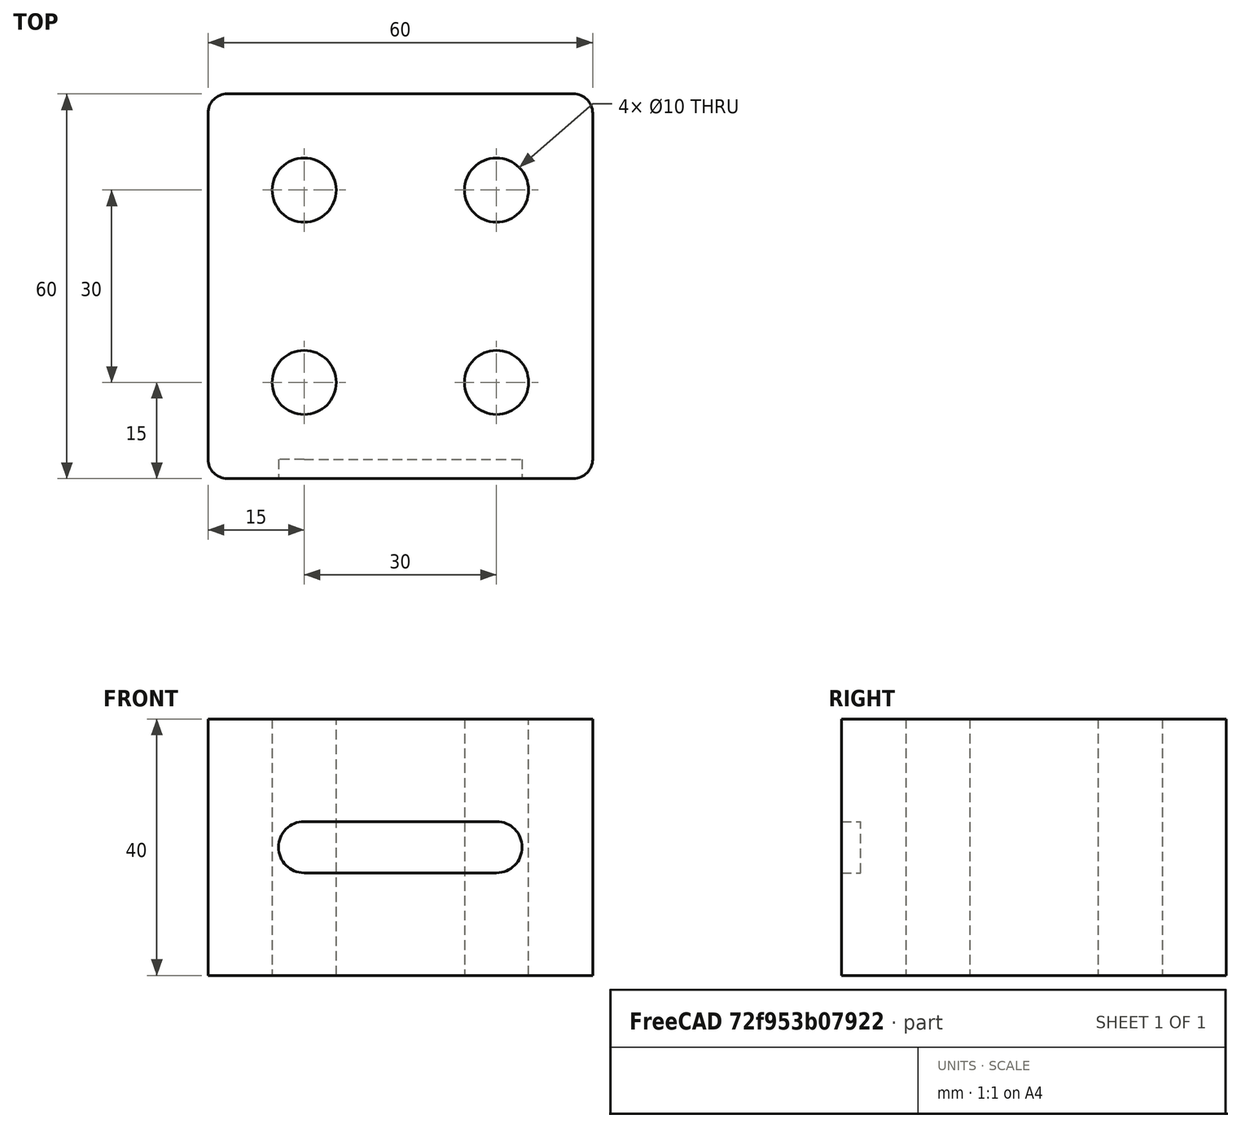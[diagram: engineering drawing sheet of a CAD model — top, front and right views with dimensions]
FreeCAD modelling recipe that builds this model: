
FCSTD DOCUMENT  (FreeCAD 1.0R39319 (Git))
Label: block(2D drawing)
License: All rights reserved
LicenseURL: https://en.wikipedia.org/wiki/All_rights_reserved
objects: TechDraw::DrawViewDimension×6, TechDraw::DrawProjGroupItem×4, TechDraw::DrawViewBalloon×3, Sketcher::SketchObject×2, TechDraw::DrawViewAnnotation×2, PartDesign::Pad×1, PartDesign::Pocket×1, PartDesign::Fillet×1, PartDesign::Body×1, TechDraw::DrawSVGTemplate×1, TechDraw::DrawProjGroup×1, TechDraw::DrawPage×1
note: 21 computed .brp shape members not serialized (recipe doc carries the construction recipe); baked Part::Feature solids carry a one-line shape summary decoded from their .brp

FEATURE [Sketcher::SketchObject] Sketch
  ArcFitTolerance = 1e-06
  AttachmentSupport = -> [XY_Plane]
  FullyConstrained = true
  MakeInternals = false
  MapMode = 5
  sketch-geometry (9):
    g0: LineSegment StartX=-30 StartY=30 StartZ=0 EndX=-30 EndY=-30 EndZ=0
    g1: LineSegment StartX=-30 StartY=-30 StartZ=0 EndX=30 EndY=-30 EndZ=0
    g2: LineSegment StartX=30 StartY=-30 StartZ=0 EndX=30 EndY=30 EndZ=0
    g3: LineSegment StartX=30 StartY=30 StartZ=0 EndX=-30 EndY=30 EndZ=0
    g4: GeomPoint [constr] X=0 Y=0 Z=0
    g5: Circle CenterX=-15 CenterY=15 CenterZ=0 NormalX=0 NormalY=0 NormalZ=1 AngleXU=0 Radius=5
    g6: Circle CenterX=15 CenterY=15 CenterZ=0 NormalX=0 NormalY=0 NormalZ=1 AngleXU=0 Radius=5
    g7: Circle CenterX=-15 CenterY=-15 CenterZ=0 NormalX=0 NormalY=0 NormalZ=1 AngleXU=0 Radius=5
    g8: Circle CenterX=15 CenterY=-15 CenterZ=0 NormalX=0 NormalY=0 NormalZ=1 AngleXU=0 Radius=5
  constraints (24):
    c: Coincident(g0,g1)
    c: Coincident(g1,g2)
    c: Coincident(g2,g3)
    c: Coincident(g3,g0)
    c: Vertical(g0)
    c: Vertical(g2)
    c: Horizontal(g1)
    c: Horizontal(g3)
    c: Symmetric(g2,g0,g4)
    c: Coincident(g4,g-1)
    c: DistanceX(g3,g3) = 60
    c: Equal(g3,g2)
    c: Distance(g5,g3) = 15
    c: Distance(g5,g0) = 15
    c: Diameter(g5) = 10
    c: Vertical(g5,g7)
    c: Horizontal(g7,g8)
    c: Vertical(g6,g8)
    c: Distance(g6,g3) = 15
    c: Distance(g8,g2) = 15
    c: Distance(g7,g1) = 15
    c: Equal(g5,g6)
    c: Equal(g6,g8)
    c: Equal(g8,g7)
FEATURE [PartDesign::Pad] Pad
  Direction = (0,0,1)
  Length = 40
  Length2 = 10
  Profile = -> Sketch
  ReferenceAxis = -> Sketch [N_Axis]
  Refine = true
  Suppressed = false
  Type = 0
FEATURE [Sketcher::SketchObject] Sketch001
  ArcFitTolerance = 1e-06
  AttachmentSupport = -> [Pad]
  FullyConstrained = true
  MakeInternals = false
  MapMode = 5
  Placement = pos=(0,-30,0) rot=(1,0,0;1.5708rad)
  sketch-geometry (4):
    g0: ArcOfCircle CenterX=-15 CenterY=20 CenterZ=0 NormalX=0 NormalY=0 NormalZ=1 AngleXU=0 Radius=4 StartAngle=1.5708 EndAngle=4.71239
    g1: ArcOfCircle CenterX=15 CenterY=20 CenterZ=0 NormalX=0 NormalY=0 NormalZ=1 AngleXU=0 Radius=4 StartAngle=4.71239 EndAngle=7.85398
    g2: LineSegment StartX=-15 StartY=24 StartZ=0 EndX=15 EndY=24 EndZ=0
    g3: LineSegment StartX=-15 StartY=16 StartZ=0 EndX=15 EndY=16 EndZ=0
  constraints (10):
    c: Tangent(g0,g2) = 1.5708
    c: Tangent(g0,g3) = -1.5708
    c: Tangent(g1,g2) = 1.5708
    c: Tangent(g1,g3) = -1.5708
    c: Equal(g0,g1)
    c: Horizontal(g3)
    c: Radius(g0) = 4
    c: DistanceX(g0,g1) = 30
    c: DistanceY(g-1,g1) = 20
    c: Distance(g1,g-2) = 15
FEATURE [PartDesign::Pocket] Pocket
  BaseFeature = -> Pad
  Direction = (0,1,-2e-16)
  Length = 3
  Length2 = 5
  Profile = -> Sketch001
  ReferenceAxis = -> Sketch001 [N_Axis]
  Refine = true
  Suppressed = false
  Type = 0
FEATURE [PartDesign::Fillet] Fillet
  Base = -> Pocket [Edge10,Edge5,Edge2,Edge1]
  BaseFeature = -> Pocket
  Radius = 3
  Refine = true
  SupportTransform = false
  Suppressed = false
  UseAllEdges = false
FEATURE [PartDesign::Body] Body
  AllowCompound = false
  Group = -> [Sketch,Pad,Sketch001,Pocket,Fillet]
  Origin = -> Origin
  Tip = -> Fillet
FEATURE [TechDraw::DrawSVGTemplate] Template
  EditableTexts = AuthorName=AUTHOR NAME; CheckDate=CHECK DATE; CreationDate=29-11-2025; DrawingNumber=NUMBER; FC-Title=block(2D drawing); SheetNumber=1 / 1; Subtitle=SUBTITLE; SupervisorName=SUPERVISOR NAME; Weight=WEIGHT; scale=1 : 1
  Height = 297
  Orientation = 1
  Template = D:/New folder/FreeCAD 1.0/data/Mod/TechDraw/Templates/A3_Landscape_TD.svg
  Width = 420
FEATURE [TechDraw::DrawProjGroupItem] View  label="Front"
  CoarseView = false
  Direction = (0,-1,0)
  Focus = 100
  HardHidden = false
  IsoCount = 0
  IsoHidden = false
  IsoVisible = false
  LockPosition = true
  Perspective = false
  Rotation = 0
  RotationVector = (1,0,0)
  ScaleType = 2
  ScrubCount = 1
  SeamHidden = false
  SeamVisible = false
  SmoothHidden = false
  SmoothVisible = true
  Source = -> [Body]
  Type = 0
  X = 0
  XDirection = (1,0,0)
  Y = 0
FEATURE [TechDraw::DrawProjGroupItem] ProjItem  label="Top"
  CoarseView = false
  Direction = (0,0,1)
  Focus = 100
  HardHidden = false
  IsoCount = 0
  IsoHidden = false
  IsoVisible = false
  LockPosition = false
  Perspective = false
  Rotation = 0
  RotationVector = (1,0,0)
  ScaleType = 0
  ScrubCount = 1
  SeamHidden = false
  SeamVisible = false
  SmoothHidden = false
  SmoothVisible = true
  Source = -> [Body]
  Type = 4
  X = 0
  XDirection = (1,0,0)
  Y = -85.1074
FEATURE [TechDraw::DrawProjGroupItem] ProjItem001  label="Left"
  CoarseView = false
  Direction = (-1,-1e-16,0)
  Focus = 100
  HardHidden = false
  IsoCount = 0
  IsoHidden = false
  IsoVisible = false
  LockPosition = false
  Perspective = false
  Rotation = 0
  RotationVector = (1,0,0)
  ScaleType = 0
  ScrubCount = 1
  SeamHidden = false
  SeamVisible = false
  SmoothHidden = false
  SmoothVisible = true
  Source = -> [Body]
  Type = 1
  X = 96.1838
  XDirection = (1e-16,-1,0)
  Y = 0
FEATURE [TechDraw::DrawProjGroupItem] ProjItem002  label="FrontTopLeft"
  CoarseView = false
  Direction = (-0.57735,-0.57735,0.57735)
  Focus = 100
  HardHidden = false
  IsoCount = 0
  IsoHidden = false
  IsoVisible = false
  LockPosition = false
  Perspective = false
  Rotation = 0
  RotationVector = (1,0,0)
  ScaleType = 0
  ScrubCount = 1
  SeamHidden = false
  SeamVisible = false
  SmoothHidden = false
  SmoothVisible = true
  Source = -> [Body]
  Type = 6
  X = 96.1838
  XDirection = (0.707107,-0.707107,0)
  Y = -85.1074
FEATURE [TechDraw::DrawProjGroup] ProjGroup
  Anchor = -> View
  AutoDistribute = true
  LockPosition = false
  ProjectionType = 0
  Rotation = 0
  ScaleType = 0
  Source = -> [Body]
  Views = -> [View,ProjItem,ProjItem001,ProjItem002]
  X = 96.1951
  Y = 236.265
  spacingX = 25
  spacingY = 25
FEATURE [TechDraw::DrawViewDimension] Dimension
  AngleOverride = false
  Arbitrary = false
  ArbitraryTolerances = false
  BoxCorners = (2) [(-30,-20,-1e-07),(30,20,1e-07)]
  EqualTolerance = true
  ExtensionAngle = 0
  FormatSpec = %.2w
  FormatSpecOverTolerance = %+.2w
  FormatSpecUnderTolerance = %+.2w
  Inverted = false
  LineAngle = 0
  LockPosition = false
  MeasureType = 1
  OverTolerance = 0
  References2D = -> [View]
  Rotation = 0
  ScaleType = 0
  TheoreticalExact = false
  Type = 2
  UnderTolerance = 0
  X = 32.8535
  Y = 3.01053
FEATURE [TechDraw::DrawViewDimension] Dimension001
  AngleOverride = false
  Arbitrary = false
  ArbitraryTolerances = false
  BoxCorners = (2) [(-30,-20,-1e-07),(30,20,1e-07)]
  EqualTolerance = true
  ExtensionAngle = 0
  FormatSpec = %.2w
  FormatSpecOverTolerance = %+.2w
  FormatSpecUnderTolerance = %+.2w
  Inverted = false
  LineAngle = 0
  LockPosition = false
  MeasureType = 1
  OverTolerance = 0
  References2D = -> [View]
  Rotation = 0
  ScaleType = 0
  TheoreticalExact = false
  Type = 1
  UnderTolerance = 0
  X = 0
  Y = 36.881
FEATURE [TechDraw::DrawViewDimension] Dimension002
  AngleOverride = false
  Arbitrary = false
  ArbitraryTolerances = false
  BoxCorners = (2) [(-30,-20,-1e-07),(30,20,1e-07)]
  EqualTolerance = true
  ExtensionAngle = 0
  FormatSpec = R%.2w
  FormatSpecOverTolerance = %+.2w
  FormatSpecUnderTolerance = %+.2w
  Inverted = false
  LineAngle = 0
  LockPosition = false
  MeasureType = 1
  OverTolerance = 0
  References2D = -> [View]
  Rotation = 0
  ScaleType = 0
  TheoreticalExact = false
  Type = 4
  UnderTolerance = 0
  X = 34.5857
  Y = 39.578
FEATURE [TechDraw::DrawViewDimension] Dimension003
  AngleOverride = false
  Arbitrary = false
  ArbitraryTolerances = false
  BoxCorners = (2) [(-30,-20,-1e-07),(30,20,1e-07)]
  EqualTolerance = true
  ExtensionAngle = 0
  FormatSpec = %.2w
  FormatSpecOverTolerance = %+.2w
  FormatSpecUnderTolerance = %+.2w
  Inverted = false
  LineAngle = 0
  LockPosition = false
  MeasureType = 1
  OverTolerance = 0
  References2D = -> [View]
  Rotation = 0
  ScaleType = 0
  TheoreticalExact = false
  Type = 0
  UnderTolerance = 0
  X = 40.1788
  Y = -23.8341
FEATURE [TechDraw::DrawViewDimension] Dimension004
  AngleOverride = false
  Arbitrary = false
  ArbitraryTolerances = false
  BoxCorners = (2) [(-30,-30,0),(30,30,0)]
  EqualTolerance = true
  ExtensionAngle = 0
  FormatSpec = ⌀%.2w
  FormatSpecOverTolerance = %+.2w
  FormatSpecUnderTolerance = %+.2w
  Inverted = false
  LineAngle = 0
  LockPosition = false
  MeasureType = 1
  OverTolerance = 0
  References2D = -> [ProjItem]
  Rotation = 0
  ScaleType = 0
  TheoreticalExact = false
  Type = 5
  UnderTolerance = 0
  X = -6.56778
  Y = 41.7935
FEATURE [TechDraw::DrawViewDimension] Dimension005
  AngleOverride = false
  Arbitrary = false
  ArbitraryTolerances = false
  BoxCorners = (2) [(-30,-20,-1e-07),(30,20,1e-07)]
  EqualTolerance = false
  ExtensionAngle = 0
  FormatSpec = %.2w
  FormatSpecOverTolerance = %+.2w
  FormatSpecUnderTolerance = %+.2w
  Inverted = false
  LineAngle = 0
  LockPosition = false
  MeasureType = 1
  OverTolerance = 0.3
  References2D = -> [ProjItem001]
  Rotation = 0
  ScaleType = 0
  TheoreticalExact = false
  Type = 2
  UnderTolerance = 0
  X = 40.56
  Y = 3.33273
FEATURE [TechDraw::DrawViewAnnotation] Annotation
  Font = osifont
  LineSpace = 100
  LockPosition = false
  MaxWidth = -1
  Rotation = 0
  ScaleType = 0
  Text = 2D Drawing of a block
  TextSize = 5
  TextStyle = 0
  X = 329.81
  Y = 269.072
FEATURE [TechDraw::DrawViewAnnotation] Annotation001
  Font = osifont
  LineSpace = 100
  LockPosition = false
  MaxWidth = -1
  Rotation = 0
  ScaleType = 0
  Text = 4 holes of  ⌀ 10 mm
  TextSize = 5
  TextStyle = 0
  X = 37.6309
  Y = 189.704
FEATURE [TechDraw::DrawViewBalloon] Balloon
  BubbleShape = 5
  EndType = 6
  EndTypeScale = 1
  KinkLength = 5
  LockPosition = false
  OriginX = -15.7369
  OriginY = 19.4046
  Rotation = 0
  ScaleType = 0
  ShapeScale = 1
  SourceView = -> View
  Text = A
  TextWrapLen = -1
  X = -39.5236
  Y = 39.2855
FEATURE [TechDraw::DrawViewBalloon] Balloon001
  BubbleShape = 5
  EndType = 6
  EndTypeScale = 1
  KinkLength = 5
  LockPosition = false
  OriginX = 11.2925
  OriginY = -30.6105
  Rotation = 0
  ScaleType = 0
  ShapeScale = 1
  SourceView = -> ProjItem
  Text = B
  TextWrapLen = -1
  X = -4.36929
  Y = -55.5645
FEATURE [TechDraw::DrawViewBalloon] Balloon002
  BubbleShape = 5
  EndType = 6
  EndTypeScale = 1
  KinkLength = 5
  LockPosition = false
  OriginX = 13.9477
  OriginY = 19.9609
  Rotation = 0
  ScaleType = 0
  ShapeScale = 1
  SourceView = -> ProjItem001
  Text = C
  TextWrapLen = -1
  X = 33.9477
  Y = 39.9609
FEATURE [TechDraw::DrawPage] Page
  KeepUpdated = true
  NextBalloonIndex = 4
  ProjectionType = 0
  Template = -> Template
  Views = -> [ProjGroup,Dimension,Dimension001,Dimension002,Dimension003,Dimension004,Dimension005,Annotation,Annotation001,Balloon,Balloon001,Balloon002]
